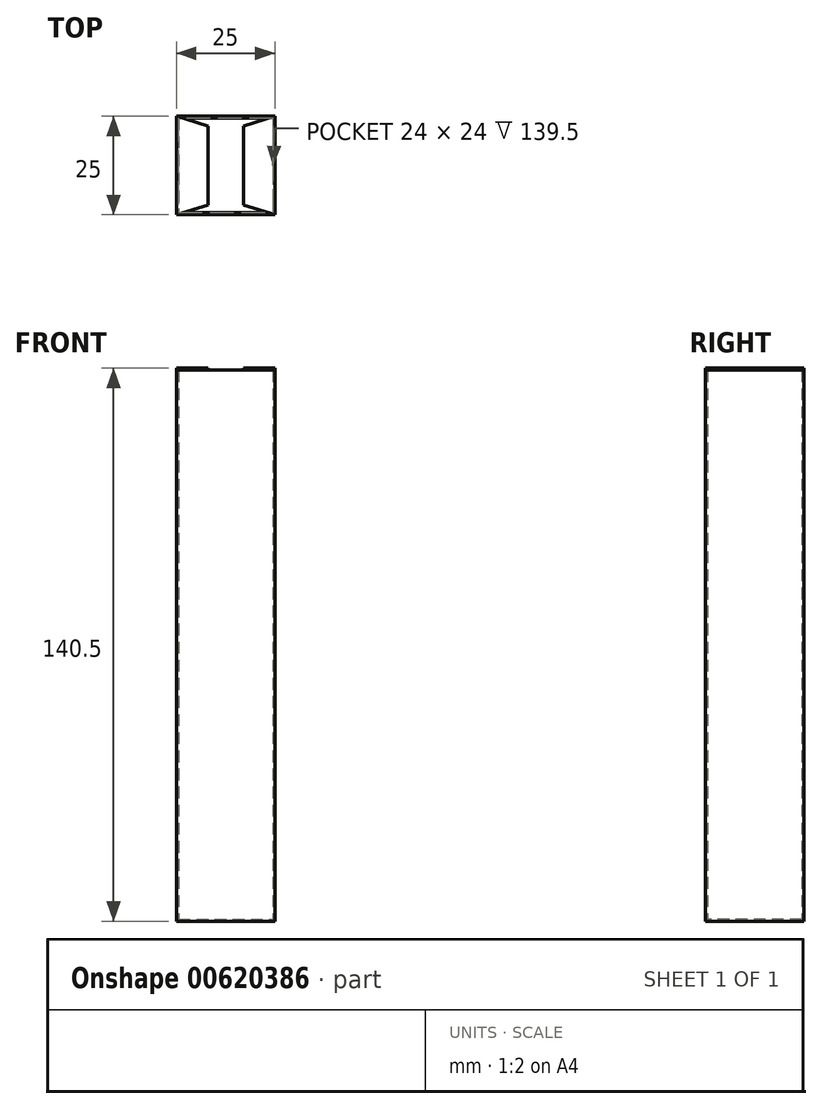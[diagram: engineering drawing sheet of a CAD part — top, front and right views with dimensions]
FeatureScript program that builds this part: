
annotation { "Feature Type Name" : "Feature", "Feature Type Description" : "" }
export const myFeature = defineFeature(function(context is Context, id is Id, definition is map)
    precondition{}
    {
        {
            var Q0;
            Q0=qCreatedBy(makeId("Top.planeOp"),FACE);
            var sketch = newSketch(context, id + "F0", { "sketchPlane" : qUnion([Q0])});
            skPoint(sketch, "E0.middle", {"position": v(0, 0) * mm});
            skLineSegment(sketch, "E1.bottom", {"start": v(-12.5, 12.5) * mm, "end": v(12.5, 12.5) * mm});
            skLineSegment(sketch, "E1.top", {"start": v(-12.5, -12.5) * mm, "end": v(12.5, -12.5) * mm});
            skLineSegment(sketch, "E1.left", {"start": v(-12.5, 12.5) * mm, "end": v(-12.5, -12.5) * mm});
            skLineSegment(sketch, "E1.right", {"start": v(12.5, 12.5) * mm, "end": v(12.5, -12.5) * mm});
            skSolve(sketch);
        }
        {
            var Q0;
            Q0 = qSketchRegion(id + "F0", true);
            extrude(context, id + "F1", {"entities" : qUnion([Q0]), "depth" : 140 * mm, "offsetDistance" : 25 * mm});
        }
        {
            var Q0;
            Q0=makeQuery(id+"F1.opExtrude","CAP_FACE",FACE,{"disambiguationData":[OSD([sQuery(id+"F0.wireOp",EDGE,"E1.bottom"),sQuery(id+"F0.wireOp",EDGE,"E1.top"),sQuery(id+"F0.wireOp",EDGE,"E1.left"),sQuery(id+"F0.wireOp",EDGE,"E1.right")])],"isStart":false});
            shell(context, id + "F2", {"entities" : qUnion([Q0]), "thickness" : 0.5 * mm});
        }
        {
            var Q0;
            Q0=makeQuery(id+"F1.opExtrude","CAP_FACE",FACE,{"disambiguationData":[OSD([sQuery(id+"F0.wireOp",EDGE,"E1.bottom"),sQuery(id+"F0.wireOp",EDGE,"E1.top"),sQuery(id+"F0.wireOp",EDGE,"E1.left"),sQuery(id+"F0.wireOp",EDGE,"E1.right")])],"isStart":false});
            var sketch = newSketch(context, id + "F3", { "sketchPlane" : qUnion([Q0])});
            skLineSegment(sketch, "E2", {"start": v(-12.5, 12.5) * mm, "end": v(-4.5, 10) * mm});
            skLineSegment(sketch, "E3", {"start": v(-4.5, 10) * mm, "end": v(-4.5, -10) * mm});
            skLineSegment(sketch, "E4", {"start": v(-4.5, -10) * mm, "end": v(-12.5, -12.5) * mm});
            skLineSegment(sketch, "E5", {"start": v(-12.5, -12.5) * mm, "end": v(-12.5, 12.5) * mm});
            skSolve(sketch);
        }
        {
            var Q0;
            Q0 = qSketchRegion(id + "F3", true);
            extrude(context, id + "F4", {"entities" : qUnion([Q0]), "depth" : 0.5 * mm, "offsetDistance" : 25 * mm});
        }
        {
            var Q0;
            Q0=makeQuery(id+"F4.opExtrude","SWEPT_BODY",BODY,{"disambiguationData":[OSD([sQuery(id+"F3.wireOp",EDGE,"E2"),sQuery(id+"F3.wireOp",EDGE,"E3"),sQuery(id+"F3.wireOp",EDGE,"E4"),sQuery(id+"F3.wireOp",EDGE,"E5")])]});
            var Q1;
            Q1=qCreatedBy(makeId("Right.planeOp"),FACE);
            mirror(context, id + "F5", {"entities" : qUnion([Q0]), "mirrorPlane" : qUnion([Q1])});
        }
    });
